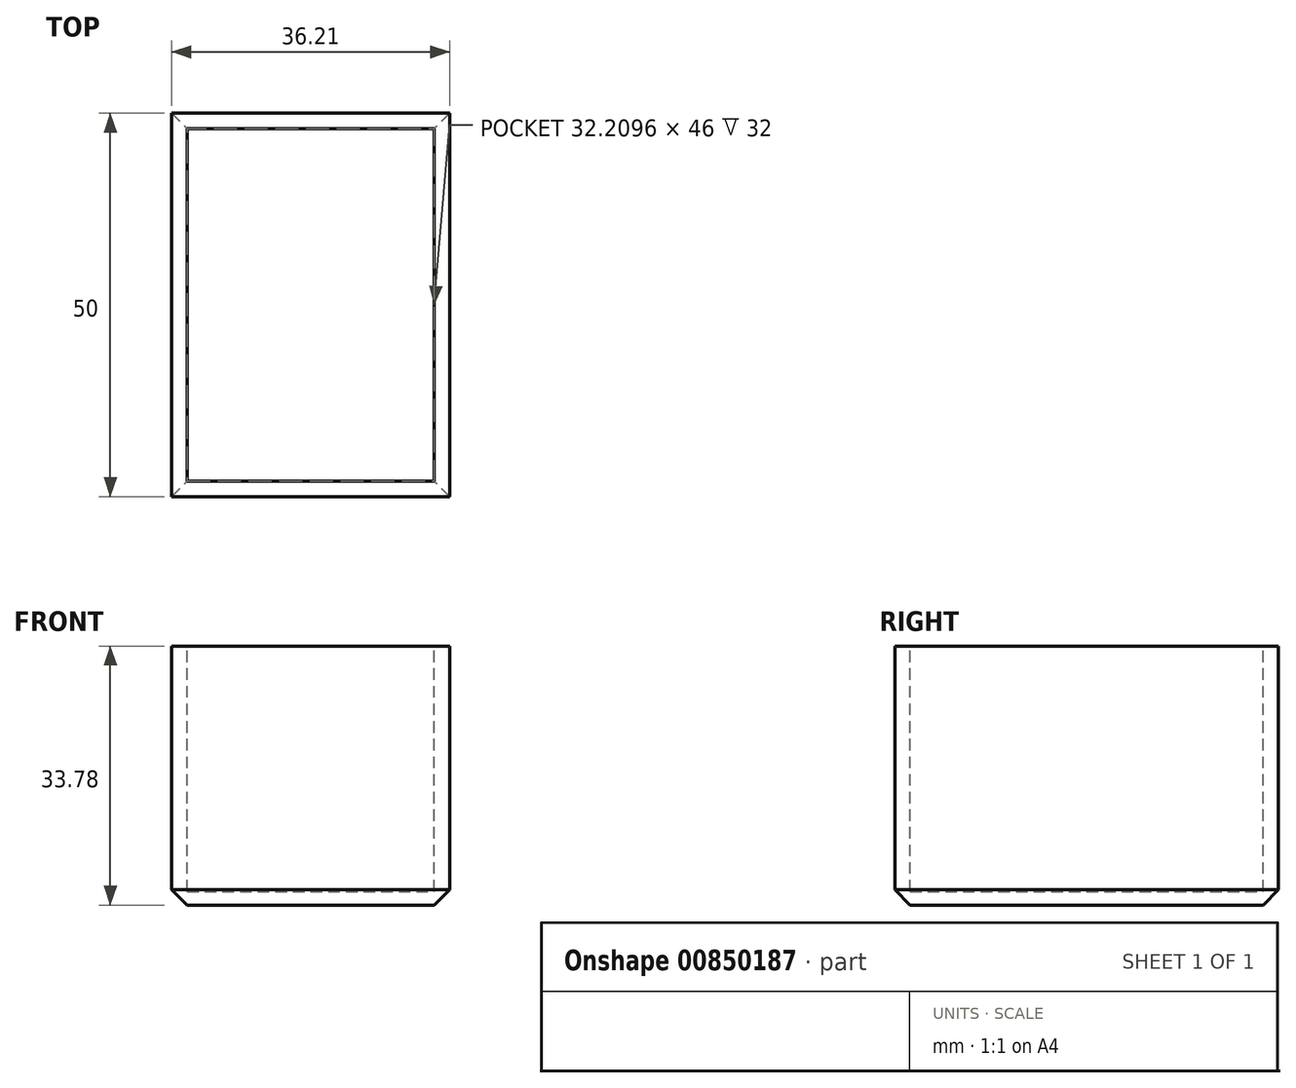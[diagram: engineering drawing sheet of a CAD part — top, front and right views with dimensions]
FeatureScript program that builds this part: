
annotation { "Feature Type Name" : "Feature", "Feature Type Description" : "" }
export const myFeature = defineFeature(function(context is Context, id is Id, definition is map)
    precondition{}
    {
        {
            var Q0;
            Q0=qCreatedBy(makeId("Front.planeOp"),FACE);
            var sketch = newSketch(context, id + "F0", { "sketchPlane" : qUnion([Q0])});
            skLineSegment(sketch, "E0.bottom", {"start": v(0, 0) * mm, "end": v(36.2, 0) * mm});
            skLineSegment(sketch, "E0.top", {"start": v(0, 33.78) * mm, "end": v(36.2, 33.78) * mm});
            skLineSegment(sketch, "E0.left", {"start": v(0, 0) * mm, "end": v(0, 33.78) * mm});
            skLineSegment(sketch, "E0.right", {"start": v(36.2, 0) * mm, "end": v(36.2, 33.78) * mm});
            skSolve(sketch);
        }
        {
            var Q0;
            Q0 = qSketchRegion(id + "F0", true);
            extrude(context, id + "F1", {"entities" : qUnion([Q0]), "depth" : 50 * mm, "offsetDistance" : 25 * mm});
        }
        {
            var Q0;
            Q0=makeQuery(id+"F1.opExtrude","SWEPT_FACE",FACE,{"disambiguationData":[OSD([sQuery(id+"F0.wireOp",EDGE,"E0.top")])]});
            var sketch = newSketch(context, id + "F2", { "sketchPlane" : qUnion([Q0])});
            skLineSegment(sketch, "E1.bottom", {"start": v(2, -48) * mm, "end": v(34.2, -48) * mm});
            skLineSegment(sketch, "E1.top", {"start": v(2, -2) * mm, "end": v(34.2, -2) * mm});
            skLineSegment(sketch, "E1.left", {"start": v(2, -48) * mm, "end": v(2, -2) * mm});
            skLineSegment(sketch, "E1.right", {"start": v(34.2, -48) * mm, "end": v(34.2, -2) * mm});
            skSolve(sketch);
        }
        {
            var Q0;
            Q0 = qSketchRegion(id + "F2", true);
            extrude(context, id + "F3", {"entities" : qUnion([Q0]), "operationType" : NewBodyOperationType.REMOVE, "oppositeDirection" : true, "depth" : 32 * mm, "offsetDistance" : 25 * mm});
        }
        {
            var Q0;
            Q0=makeQuery(id+"F1.opExtrude","CAP_EDGE",EDGE,{"disambiguationData":[OSD([sQuery(id+"F0.wireOp",EDGE,"E0.bottom")])],"isStart":true});
            var Q1;
            Q1=makeQuery(id+"F1.opExtrude","SWEPT_FACE",FACE,{"disambiguationData":[OSD([sQuery(id+"F0.wireOp",EDGE,"E0.bottom")])]});
            chamfer(context, id + "F4", {"entities" : qUnion([Q0, Q1]), "width" : 2 * mm, "tangentPropagation" : true});
        }
    });
